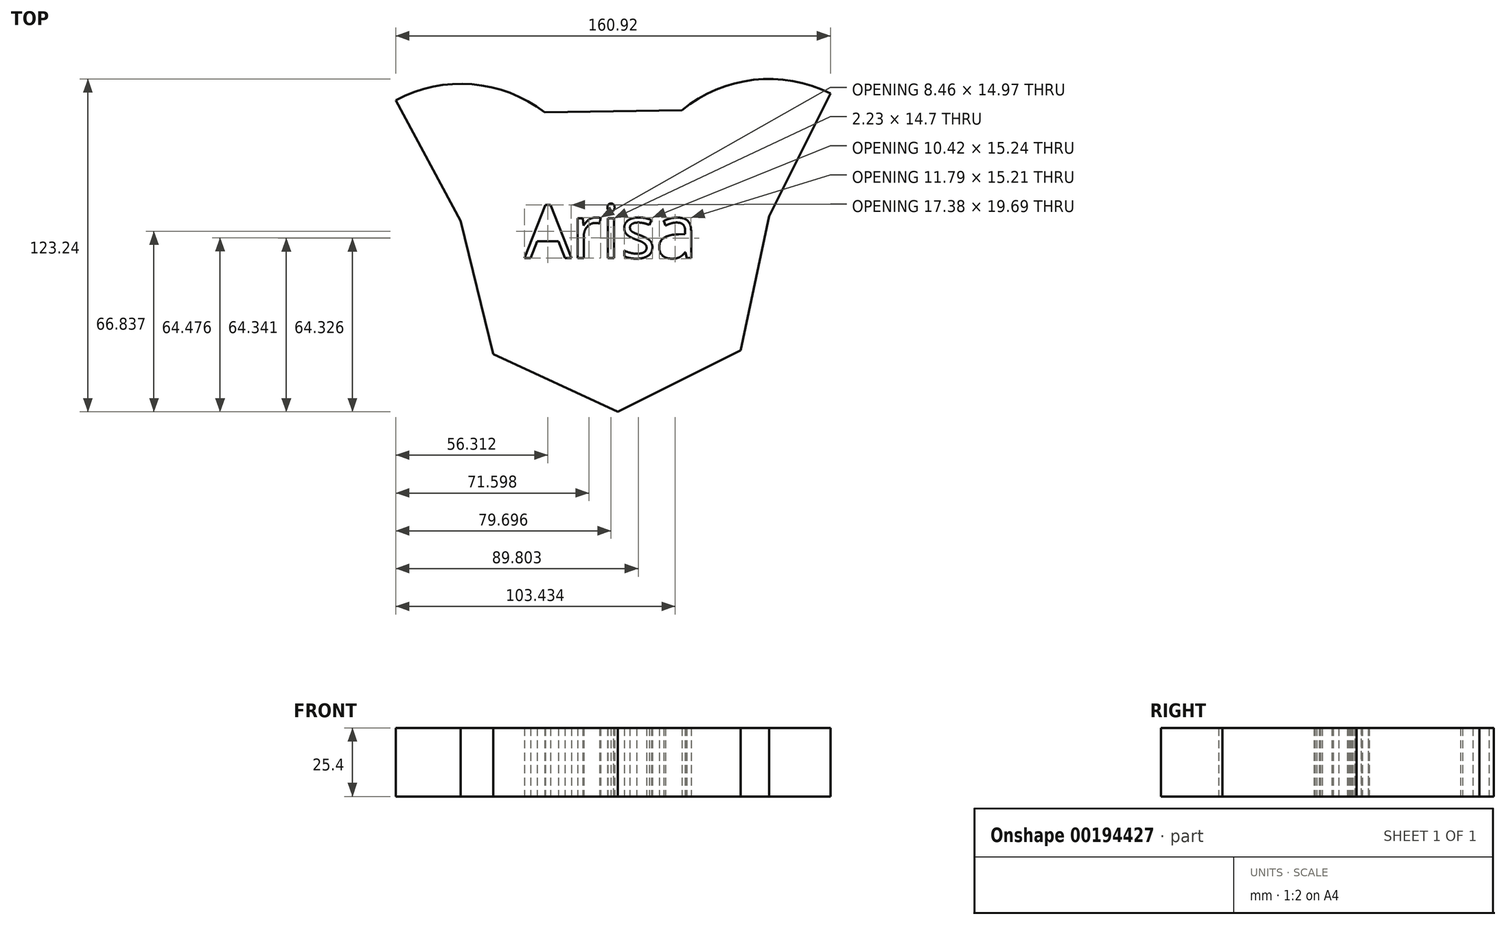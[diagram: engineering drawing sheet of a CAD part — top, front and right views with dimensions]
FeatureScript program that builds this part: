
annotation { "Feature Type Name" : "Feature", "Feature Type Description" : "" }
export const myFeature = defineFeature(function(context is Context, id is Id, definition is map)
    precondition{}
    {
        {
            var Q0;
            Q0=qCreatedBy(makeId("Top.planeOp"),FACE);
            var sketch = newSketch(context, id + "F0", { "sketchPlane" : qUnion([Q0])});
            skCircle(sketch, "E0.cCircle", {"center": v(0, 0) * mm, "radius": 52.74 * mm, "construction": true});
            skLineSegment(sketch, "E0.0", {"start": v(-57.27, 12.14) * mm, "end": v(-26.21, 52.34) * mm});
            skLineSegment(sketch, "E0.1", {"start": v(-26.21, 52.34) * mm, "end": v(24.58, 53.13) * mm});
            skLineSegment(sketch, "E0.2", {"start": v(24.58, 53.13) * mm, "end": v(56.86, 13.9) * mm});
            skLineSegment(sketch, "E0.3", {"start": v(56.86, 13.9) * mm, "end": v(46.33, -35.79) * mm});
            skLineSegment(sketch, "E0.4", {"start": v(46.33, -35.79) * mm, "end": v(0.9, -58.53) * mm});
            skLineSegment(sketch, "E0.5", {"start": v(0.9, -58.53) * mm, "end": v(-45.2, -37.2) * mm});
            skLineSegment(sketch, "E0.6", {"start": v(-45.2, -37.2) * mm, "end": v(-57.27, 12.14) * mm});
            skPoint(sketch, "E0.0.midPoint", {"position": v(-41.74, 32.24) * mm});
            skText(sketch, "E1", { "text": "Arisa", "fontName": "OpenSans-Regular.ttf"});
            const initialGuessF0  = {"E1": [-0.03374, -0.00154, 1, 0, 0.01978]};
            skSetInitialGuess(sketch, initialGuessF0);
            skSolve(sketch);
        }
        {
            var Q0;
            Q0=makeQuery(id+"F0.imprint","IMPRINT",FACE,{"disambiguationData":[TD([[makeQuery(id+"F0.imprint","IMPRINT",EDGE,{"derivedFrom":sQuery(id+"F0.wireOp",EDGE,"E0.0")}),-1.0]])]});
            extrude(context, id + "F1", {"entities" : qUnion([Q0]), "depth" : 25.4 * mm});
        }
        {
            var Q0;
            Q0=makeQuery(id+"F1.opExtrude","SWEPT_FACE",FACE,{"disambiguationData":[OSD([sQuery(id+"F0.wireOp",EDGE,"E0.2")])]});
            var Q1;
            Q1=makeQuery(id+"F1.opExtrude","SWEPT_EDGE",EDGE,{"disambiguationData":[OSD([sQuery(id+"F0.wireOp",EDGE,"E0.2"),sQuery(id+"F0.wireOp",EDGE,"E0.3")])]});
            revolve(context, id + "F2", {"operationType" : NewBodyOperationType.ADD, "entities" : qUnion([Q0]), "axis" : qUnion([Q1]), "revolveType" : RevolveType.ONE_DIRECTION, "angle" : 66 * degree});
        }
        {
            var Q0;
            Q0=makeQuery(id+"F1.opExtrude","SWEPT_FACE",FACE,{"disambiguationData":[OSD([sQuery(id+"F0.wireOp",EDGE,"E0.0")])]});
            var Q1;
            Q1=makeQuery(id+"F1.opExtrude","SWEPT_EDGE",EDGE,{"disambiguationData":[OSD([sQuery(id+"F0.wireOp",EDGE,"E0.0"),sQuery(id+"F0.wireOp",EDGE,"E0.6")])]});
            revolve(context, id + "F3", {"operationType" : NewBodyOperationType.ADD, "entities" : qUnion([Q0]), "axis" : qUnion([Q1]), "revolveType" : RevolveType.ONE_DIRECTION, "oppositeDirection" : true, "angle" : 66 * degree});
        }
    });
